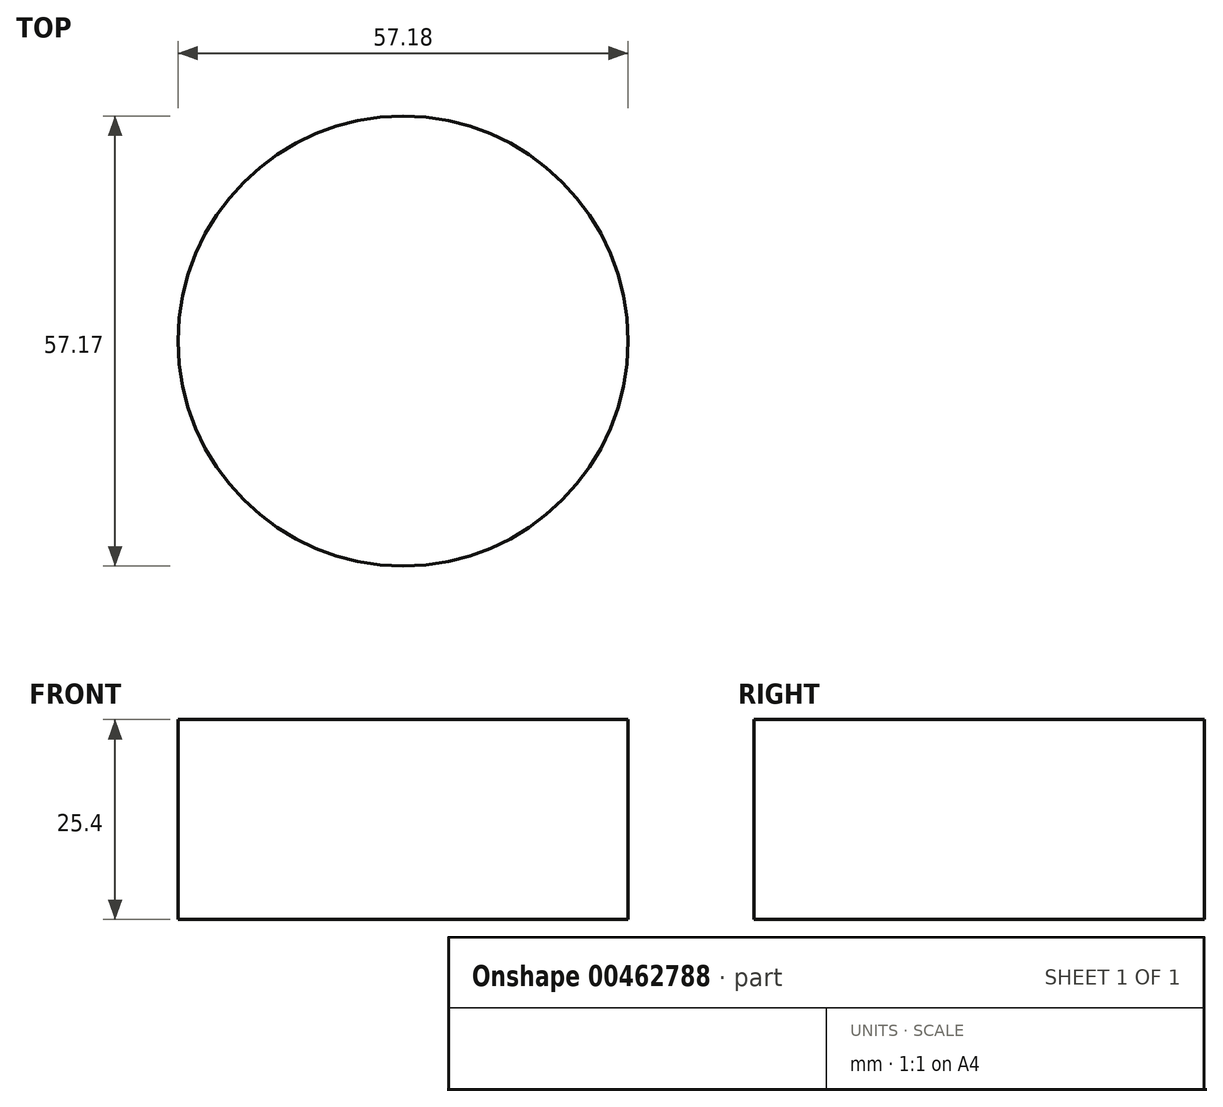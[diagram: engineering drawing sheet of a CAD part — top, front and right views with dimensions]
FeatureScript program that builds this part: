
annotation { "Feature Type Name" : "Feature", "Feature Type Description" : "" }
export const myFeature = defineFeature(function(context is Context, id is Id, definition is map)
    precondition{}
    {
        {
            var Q0;
            Q0=qCreatedBy(makeId("Top.planeOp"),FACE);
            var sketch = newSketch(context, id + "F0", { "sketchPlane" : qUnion([Q0])});
            skCircle(sketch, "E0", {"center": v(32.27, 35.61) * mm, "radius": 28.59 * mm});
            skSolve(sketch);
        }
        {
            var Q0;
            Q0 = qSketchRegion(id + "F0", true);
            extrude(context, id + "F1", {"entities" : qUnion([Q0]), "depth" : 25.4 * mm});
        }
    });
